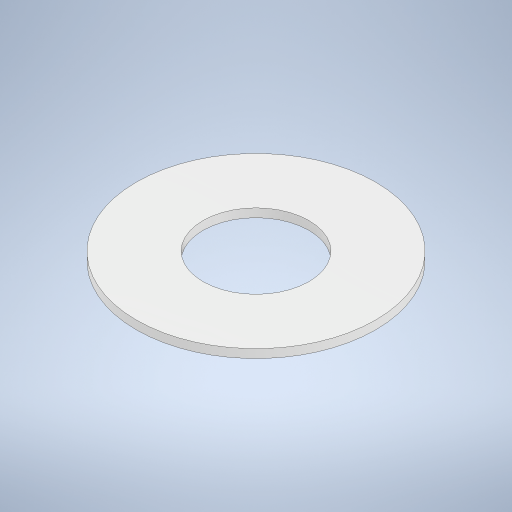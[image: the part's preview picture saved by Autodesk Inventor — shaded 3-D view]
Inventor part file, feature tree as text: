
AUTODESK INVENTOR PART (.ipt)
format: ipt  version: 2024.2 (Build 282272000, 272)  size: 235,008 bytes
history: native  units: mm
features: revolve x1, sketch x1
ambient origin geometry x8: Origin, YZ Plane, XZ Plane, XY Plane, X Axis, Y Axis, Z Axis, Center Point
bodies: Solid1 (feature_tree)
feature tree (2):
  revolve  "Revolution1"  [1 undecoded]
  sketch  "Sketch1"  dims[d5=90.0deg]
note: 1 required parameter value undecoded (feature->parameter linkage not recoverable at this tier; creation-order binding heuristic only, values carry confidence <= 0.55)
